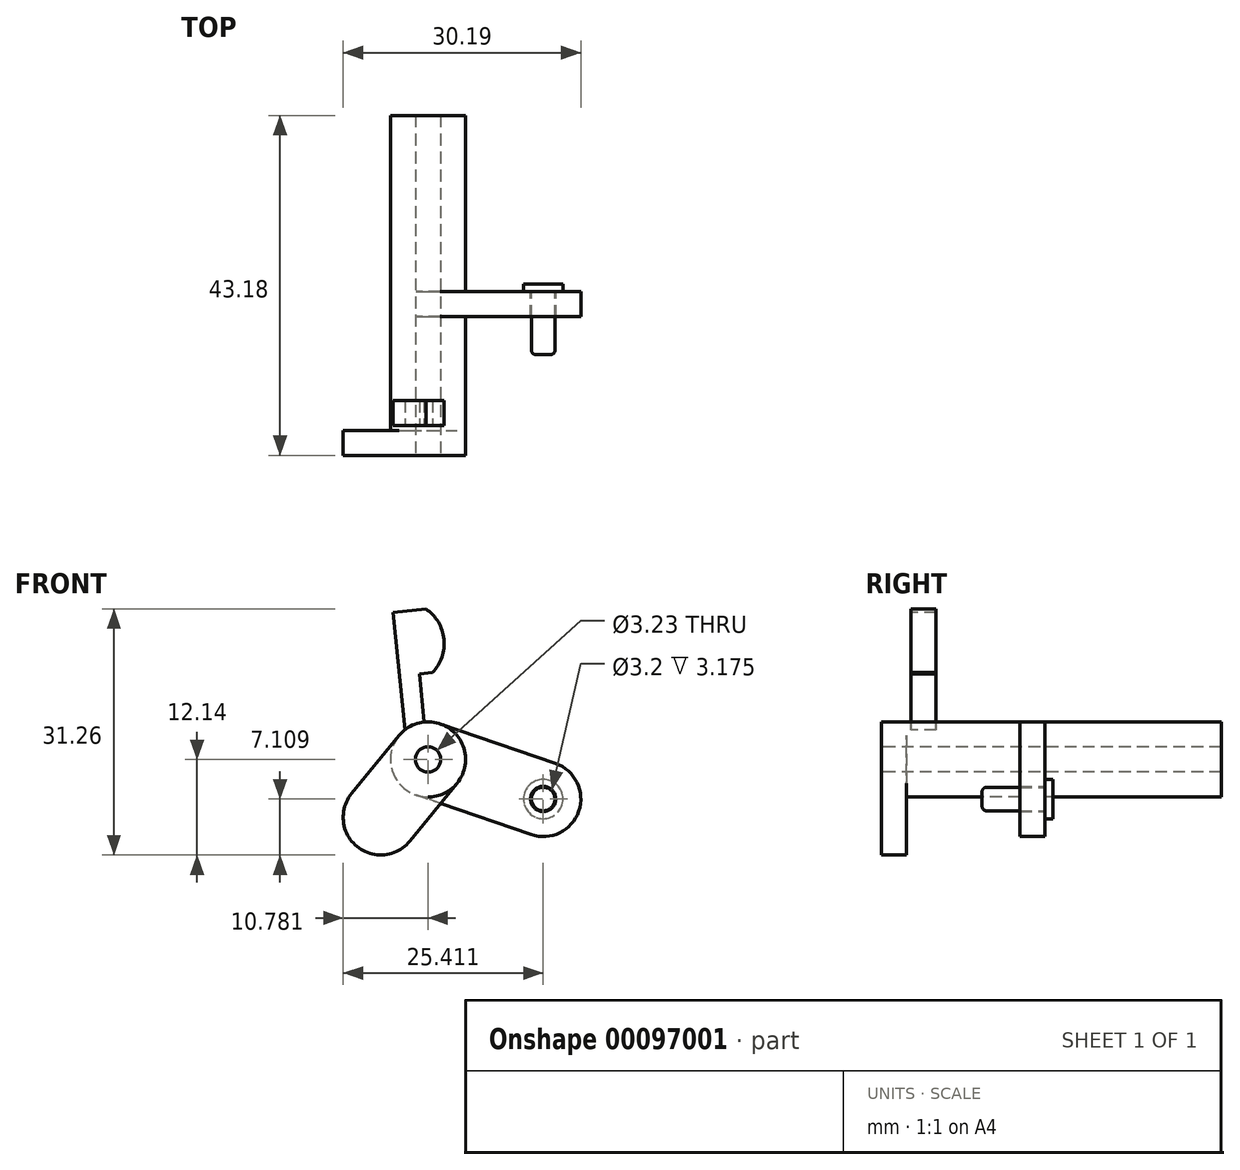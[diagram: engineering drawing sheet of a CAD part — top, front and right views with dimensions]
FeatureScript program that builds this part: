
annotation { "Feature Type Name" : "Feature", "Feature Type Description" : "" }
export const myFeature = defineFeature(function(context is Context, id is Id, definition is map)
    precondition{}
    {
        {
            var Q0;
            Q0=qCreatedBy(makeId("Front.planeOp"),FACE);
            var sketch = newSketch(context, id + "F0", { "sketchPlane" : qUnion([Q0])});
            skCircle(sketch, "E0", {"center": v(5.75, 6.18) * mm, "radius": 1.61 * mm});
            skCircle(sketch, "E1", {"center": v(14.26, 16.62) * mm, "radius": 1.61 * mm});
            skCircle(sketch, "E2", {"center": v(35.77, 9.22) * mm, "radius": 1.61 * mm});
            skArc(sketch, "E3", {"start": v(2.05, 9.2) * mm, "mid": v(2.73, 2.48) * mm, "end": v(9.44, 3.16) * mm});
            skArc(sketch, "E4", {"start": v(17.28, 20.32) * mm, "mid": v(13.78, 21.37) * mm, "end": v(10.56, 19.64) * mm});
            skArc(sketch, "E5", {"start": v(34.21, 4.7) * mm, "mid": v(40.28, 7.67) * mm, "end": v(37.32, 13.74) * mm});
            skLineSegment(sketch, "E6", {"start": v(2.05, 9.2) * mm, "end": v(10.56, 19.64) * mm});
            skLineSegment(sketch, "E7", {"start": v(9.44, 3.16) * mm, "end": v(13.98, 8.72) * mm});
            skLineSegment(sketch, "E8", {"start": v(15.81, 21.14) * mm, "end": v(37.32, 13.74) * mm});
            skLineSegment(sketch, "E9", {"start": v(29.17, 6.44) * mm, "end": v(34.21, 4.7) * mm});
            skCircle(sketch, "E10", {"center": v(24.7, 8.1) * mm, "radius": 1.61 * mm});
            skArc(sketch, "E11", {"start": v(21.68, 4.4) * mm, "mid": v(28.4, 5.08) * mm, "end": v(27.72, 11.8) * mm});
            skLineSegment(sketch, "E12", {"start": v(27.72, 11.8) * mm, "end": v(17.28, 20.32) * mm});
            skLineSegment(sketch, "E13", {"start": v(21.68, 4.4) * mm, "end": v(16.12, 8.94) * mm});
            skArc(sketch, "E14", {"start": v(16.12, 8.94) * mm, "mid": v(15, 9.27) * mm, "end": v(13.98, 8.72) * mm});
            skLineSegment(sketch, "E15", {"start": v(13.98, 35.74) * mm, "end": v(9.81, 35.32) * mm});
            skLineSegment(sketch, "E16", {"start": v(13.78, 21.37) * mm, "end": v(13.16, 27.49) * mm});
            skLineSegment(sketch, "E17", {"start": v(14.8, 27.65) * mm, "end": v(13.16, 27.49) * mm});
            skArc(sketch, "E18", {"start": v(14.8, 27.65) * mm, "mid": v(16.29, 31.89) * mm, "end": v(13.98, 35.74) * mm});
            skLineSegment(sketch, "E19", {"start": v(11.33, 20.39) * mm, "end": v(9.81, 35.32) * mm});
            skSolve(sketch);
        }
        {
            var Q0;
            Q0=qCreatedBy(makeId("Front.planeOp"),FACE);
            var sketch = newSketch(context, id + "F1", { "sketchPlane" : qUnion([Q0])});
            skCircle(sketch, "E20", {"center": v(14.26, 16.62) * mm, "radius": 4.78 * mm});
            skCircle(sketch, "E21.0", {"center": v(14.26, 16.62) * mm, "radius": 1.61 * mm});
            skSolve(sketch);
        }
        {
            var Q0;
            Q0 = qSketchRegion(id + "F1", true);
            extrude(context, id + "F2", {"entities" : qUnion([Q0]), "oppositeDirection" : true, "depth" : 40 * mm});
        }
        {
            var Q0;
            Q0=qCreatedBy(makeId("Front.planeOp"),FACE);
            var sketch = newSketch(context, id + "F3", { "sketchPlane" : qUnion([Q0])});
            skCircle(sketch, "E22.0", {"center": v(14.26, 16.62) * mm, "radius": 1.61 * mm});
            skLineSegment(sketch, "E23.0", {"start": v(4.56, 12.28) * mm, "end": v(10.56, 19.64) * mm});
            skLineSegment(sketch, "E23.2", {"start": v(11.96, 6.24) * mm, "end": v(17.96, 13.6) * mm});
            skArc(sketch, "E24", {"start": v(17.96, 13.6) * mm, "mid": v(17.28, 20.32) * mm, "end": v(10.56, 19.64) * mm});
            skPoint(sketch, "E25.orphan", {"position": v(13.98, 8.72) * mm});
            skLineSegment(sketch, "E26", {"start": v(14.26, 16.62) * mm, "end": v(5.43, 5.8) * mm, "construction": true});
            skArc(sketch, "E27", {"start": v(4.56, 12.28) * mm, "mid": v(5.24, 5.56) * mm, "end": v(11.96, 6.24) * mm});
            skPoint(sketch, "E23.1.end.orphan", {"position": v(9.44, 3.16) * mm});
            skPoint(sketch, "E23.1.start.orphan", {"position": v(2.05, 9.2) * mm});
            skSolve(sketch);
        }
        {
            var Q0;
            Q0 = qSketchRegion(id + "F3", true);
            extrude(context, id + "F4", {"entities" : qUnion([Q0]), "operationType" : NewBodyOperationType.ADD, "depth" : 3.17 * mm});
        }
        {
            var Q0;
            Q0=qCreatedBy(makeId("Front.planeOp"),FACE);
            cPlane(context, id + "F5", {"entities" : qUnion([Q0]), "cplaneType" : CPlaneType.OFFSET, "offset" : 0.6 * mm, "oppositeDirection" : true, "width" : 150 * mm, "height" : 150 * mm});
        }
        {
            var Q0;
            Q0=qCreatedBy(id+"F5.planeOp",FACE);
            var sketch = newSketch(context, id + "F6", { "sketchPlane" : qUnion([Q0])});
            skLineSegment(sketch, "E28.0", {"start": v(11.33, 20.39) * mm, "end": v(9.81, 35.32) * mm});
            skLineSegment(sketch, "E29.0", {"start": v(13.98, 35.74) * mm, "end": v(9.81, 35.32) * mm});
            skArc(sketch, "E29.1", {"start": v(14.8, 27.65) * mm, "mid": v(16.29, 31.89) * mm, "end": v(13.98, 35.74) * mm});
            skLineSegment(sketch, "E29.2", {"start": v(13.78, 21.37) * mm, "end": v(13.16, 27.49) * mm});
            skLineSegment(sketch, "E29.3", {"start": v(14.8, 27.65) * mm, "end": v(13.16, 27.49) * mm});
            skLineSegment(sketch, "E30", {"start": v(11.45, 19.12) * mm, "end": v(14, 19.12) * mm});
            skLineSegment(sketch, "E31", {"start": v(14, 19.12) * mm, "end": v(13.78, 21.37) * mm});
            skLineSegment(sketch, "E32", {"start": v(11.33, 20.39) * mm, "end": v(11.45, 19.12) * mm});
            skSolve(sketch);
        }
        {
            var Q0;
            Q0 = qSketchRegion(id + "F6", true);
            extrude(context, id + "F7", {"entities" : qUnion([Q0]), "operationType" : NewBodyOperationType.ADD, "oppositeDirection" : true, "depth" : 3.17 * mm});
        }
        {
            var Q0;
            Q0=qCreatedBy(makeId("Front.planeOp"),FACE);
            cPlane(context, id + "F8", {"entities" : qUnion([Q0]), "cplaneType" : CPlaneType.OFFSET, "offset" : 17.6 * mm, "oppositeDirection" : true, "width" : 150 * mm, "height" : 150 * mm});
        }
        {
            var Q0;
            Q0=qCreatedBy(id+"F8.planeOp",FACE);
            var sketch = newSketch(context, id + "F9", { "sketchPlane" : qUnion([Q0])});
            skLineSegment(sketch, "E33.0", {"start": v(15.81, 21.14) * mm, "end": v(30.44, 16.1) * mm});
            skLineSegment(sketch, "E34", {"start": v(27.34, 7.07) * mm, "end": v(12.7, 12.1) * mm});
            skCircle(sketch, "E35.0", {"center": v(14.26, 16.62) * mm, "radius": 1.61 * mm});
            skCircle(sketch, "E36.0", {"center": v(28.9, 11.59) * mm, "radius": 1.6 * mm});
            skArc(sketch, "E37", {"start": v(15.81, 21.14) * mm, "mid": v(9.75, 18.17) * mm, "end": v(12.7, 12.1) * mm});
            skLineSegment(sketch, "E38", {"start": v(14.26, 16.62) * mm, "end": v(39.58, 7.91) * mm, "construction": true});
            skArc(sketch, "E39", {"start": v(27.34, 7.07) * mm, "mid": v(33.4, 10.04) * mm, "end": v(30.44, 16.1) * mm});
            skSolve(sketch);
        }
        {
            var Q0;
            Q0 = qSketchRegion(id + "F9", true);
            extrude(context, id + "F10", {"entities" : qUnion([Q0]), "operationType" : NewBodyOperationType.ADD, "depth" : 3.17 * mm});
        }
        {
            var Q0;
            Q0=makeQuery(id+"F10.opExtrude","CAP_FACE",FACE,{"disambiguationData":[OSD([sQuery(id+"F9.wireOp",EDGE,"E33.0"),sQuery(id+"F9.wireOp",EDGE,"E34"),sQuery(id+"F9.wireOp",EDGE,"E35.0"),sQuery(id+"F9.wireOp",EDGE,"E36.0"),sQuery(id+"F9.wireOp",EDGE,"E37"),sQuery(id+"F9.wireOp",EDGE,"E39")])],"isStart":true});
            var sketch = newSketch(context, id + "F11", { "sketchPlane" : qUnion([Q0])});
            skCircle(sketch, "E40", {"center": v(-28.9, 11.59) * mm, "radius": 1.5 * mm});
            skSolve(sketch);
        }
        {
            var Q0;
            Q0 = qSketchRegion(id + "F11", true);
            extrude(context, id + "F12", {"entities" : qUnion([Q0]), "oppositeDirection" : true, "depth" : 8 * mm});
        }
        {
            var Q0;
            Q0=makeQuery(id+"F12.opExtrude","CAP_FACE",FACE,{"disambiguationData":[OSD([sQuery(id+"F11.wireOp",EDGE,"E40")])],"isStart":false});
            fillet(context, id + "F13", {"entities" : qUnion([Q0]), "radius" : 0.6 * mm, "tangentPropagation" : true, "allowEdgeOverflow" : false});
        }
        {
            var Q0;
            Q0=makeQuery(id+"F12.opExtrude","CAP_FACE",FACE,{"disambiguationData":[OSD([sQuery(id+"F11.wireOp",EDGE,"E40")])],"isStart":true});
            var sketch = newSketch(context, id + "F14", { "sketchPlane" : qUnion([Q0])});
            skCircle(sketch, "E41", {"center": v(-28.9, 11.59) * mm, "radius": 2.5 * mm});
            skSolve(sketch);
        }
        {
            var Q0;
            Q0 = qSketchRegion(id + "F14", true);
            extrude(context, id + "F15", {"entities" : qUnion([Q0]), "operationType" : NewBodyOperationType.ADD, "depth" : 1 * mm});
        }
    });
